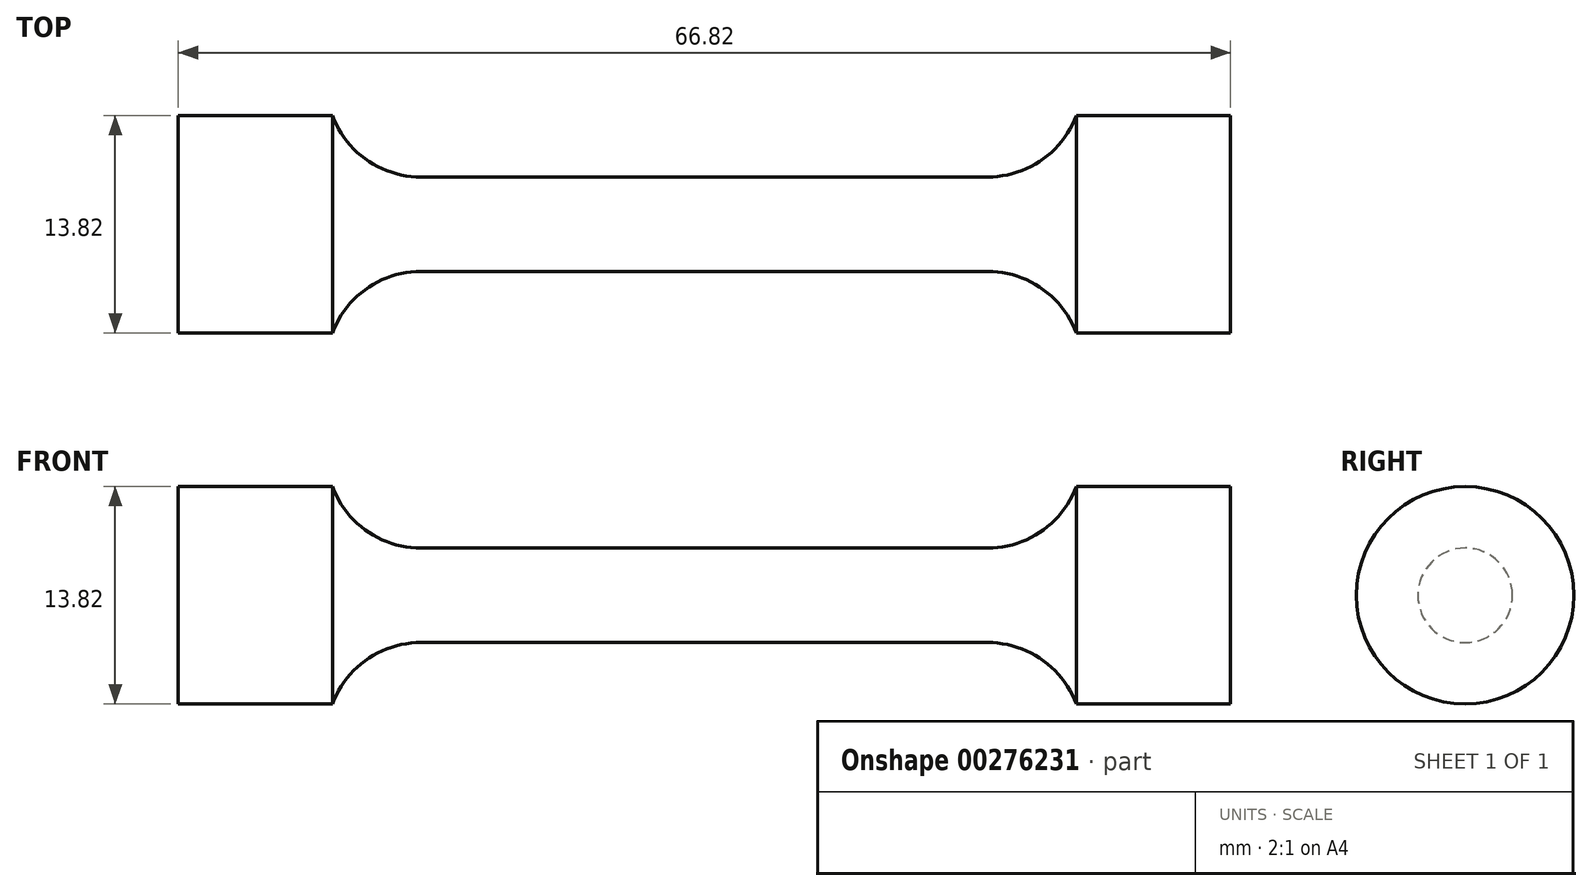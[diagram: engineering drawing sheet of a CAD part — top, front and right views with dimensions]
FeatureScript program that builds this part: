
annotation { "Feature Type Name" : "Feature", "Feature Type Description" : "" }
export const myFeature = defineFeature(function(context is Context, id is Id, definition is map)
    precondition{}
    {
        {
            var Q0;
            Q0=qCreatedBy(makeId("Front.planeOp"),FACE);
            var sketch = newSketch(context, id + "F0", { "sketchPlane" : qUnion([Q0])});
            skLineSegment(sketch, "E0", {"start": v(0, 3) * mm, "end": v(18, 3) * mm});
            skArc(sketch, "E1", {"start": v(18, 3) * mm, "mid": v(21.42, 4.07) * mm, "end": v(23.62, 6.9) * mm});
            skLineSegment(sketch, "E2", {"start": v(23.62, 6.9) * mm, "end": v(33.41, 6.9) * mm});
            skLineSegment(sketch, "E3", {"start": v(33.41, 6.9) * mm, "end": v(33.41, 0) * mm});
            skLineSegment(sketch, "E4", {"start": v(33.41, 0) * mm, "end": v(0, 0) * mm});
            skLineSegment(sketch, "E5.MirrorCS", {"start": v(0, 3) * mm, "end": v(-18, 3) * mm});
            skLineSegment(sketch, "E6.MirrorCS", {"start": v(-33.41, 0) * mm, "end": v(0, 0) * mm});
            skLineSegment(sketch, "E7.MirrorCS", {"start": v(-23.62, 6.9) * mm, "end": v(-33.41, 6.9) * mm});
            skLineSegment(sketch, "E8.MirrorCS", {"start": v(-33.41, 6.9) * mm, "end": v(-33.41, 0) * mm});
            skArc(sketch, "E9.MirrorCS", {"start": v(-18, 3) * mm, "mid": v(-21.42, 4.07) * mm, "end": v(-23.62, 6.9) * mm});
            skSolve(sketch);
        }
        {
            var Q0;
            Q0 = qSketchRegion(id + "F0", true);
            var Q1;
            Q1=sQuery(id+"F0.wireOp",EDGE,"E6.MirrorCS");
            revolve(context, id + "F1", {"entities" : qUnion([Q0]), "axis" : qUnion([Q1]), "revolveType" : RevolveType.FULL});
        }
    });
